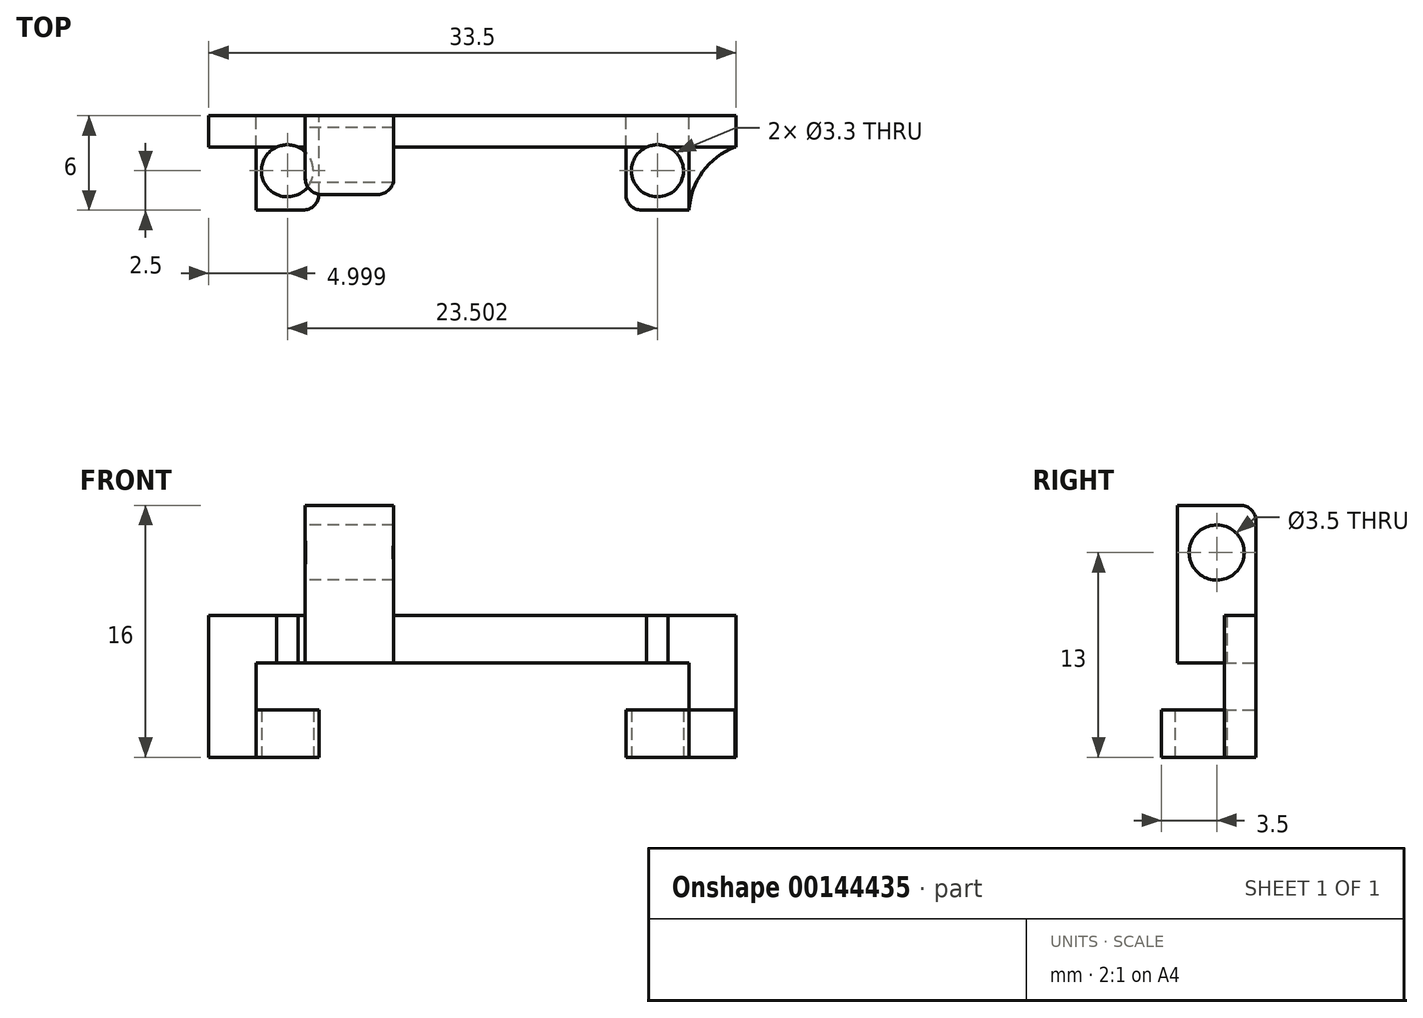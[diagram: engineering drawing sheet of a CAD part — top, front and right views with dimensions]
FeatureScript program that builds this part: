
annotation { "Feature Type Name" : "Feature", "Feature Type Description" : "" }
export const myFeature = defineFeature(function(context is Context, id is Id, definition is map)
    precondition{}
    {
        {
            var Q0;
            Q0=qCreatedBy(makeId("Front.planeOp"),FACE);
            var sketch = newSketch(context, id + "F0", { "sketchPlane" : qUnion([Q0])});
            skLineSegment(sketch, "E0.bottom", {"start": v(0, 0) * mm, "end": v(-16.75, 0) * mm});
            skLineSegment(sketch, "E0.top", {"start": v(0, 3) * mm, "end": v(-16.75, 3) * mm});
            skLineSegment(sketch, "E0.left", {"start": v(0, 0) * mm, "end": v(0, 3) * mm});
            skLineSegment(sketch, "E0.right", {"start": v(-16.75, 0) * mm, "end": v(-16.75, 3) * mm});
            skLineSegment(sketch, "E1.top", {"start": v(-16.75, 0) * mm, "end": v(-13.75, 0) * mm});
            skLineSegment(sketch, "E2.bottom", {"start": v(-13.75, 0) * mm, "end": v(-16.75, 0) * mm});
            skLineSegment(sketch, "E2.top", {"start": v(-13.75, -6) * mm, "end": v(-16.75, -6) * mm});
            skLineSegment(sketch, "E2.left", {"start": v(-13.75, 0) * mm, "end": v(-13.75, -6) * mm});
            skLineSegment(sketch, "E2.right", {"start": v(-16.75, 0) * mm, "end": v(-16.75, -6) * mm});
            skLineSegment(sketch, "E3.bottom", {"start": v(-9.75, -6) * mm, "end": v(-16.75, -6) * mm});
            skLineSegment(sketch, "E3.top", {"start": v(-9.75, -3) * mm, "end": v(-16.75, -3) * mm});
            skLineSegment(sketch, "E3.left", {"start": v(-16.75, -6) * mm, "end": v(-16.75, -3) * mm});
            skLineSegment(sketch, "E3.right", {"start": v(-9.75, -6) * mm, "end": v(-9.75, -3) * mm});
            skLineSegment(sketch, "E4.MirrorCS", {"start": v(0, 3) * mm, "end": v(16.75, 3) * mm});
            skLineSegment(sketch, "E5.MirrorCS", {"start": v(16.75, 0) * mm, "end": v(16.75, 3) * mm});
            skLineSegment(sketch, "E6.MirrorCS", {"start": v(16.75, 0) * mm, "end": v(16.75, -6) * mm});
            skLineSegment(sketch, "E7.MirrorCS", {"start": v(9.75, -3) * mm, "end": v(16.75, -3) * mm});
            skLineSegment(sketch, "E8.MirrorCS", {"start": v(9.75, -6) * mm, "end": v(9.75, -3) * mm});
            skLineSegment(sketch, "E9.MirrorCS", {"start": v(9.75, -6) * mm, "end": v(16.75, -6) * mm});
            skLineSegment(sketch, "E10.MirrorCS", {"start": v(13.75, -6) * mm, "end": v(16.75, -6) * mm});
            skLineSegment(sketch, "E11.MirrorCS", {"start": v(13.75, 0) * mm, "end": v(13.75, -6) * mm});
            skLineSegment(sketch, "E12.MirrorCS", {"start": v(0, 0) * mm, "end": v(16.75, 0) * mm});
            skSolve(sketch);
        }
        {
            var Q0;
            Q0=qSketchRegion(id+"F0",true);
            extrude(context, id + "F1", {"entities" : qUnion([Q0]), "depth" : 2 * mm});
        }
        {
            var Q0;
            Q0=makeQuery(id+"F1.opExtrude","CAP_FACE",FACE,{"disambiguationData":[OSD([sQuery(id+"F0.wireOp",EDGE,"E0.bottom"),sQuery(id+"F0.wireOp",EDGE,"E0.top"),sQuery(id+"F0.wireOp",EDGE,"aeqE6Dur-HZPA-TlM0-ftwt-VVeKIwCkpguP.bottom"),sQuery(id+"F0.wireOp",EDGE,"aeqE6Dur-HZPA-TlM0-ftwt-VVeKIwCkpguP.right"),sQuery(id+"F0.wireOp",EDGE,"3cbdc3cd-563d-4b25-9951-626386d711b80.MirrorCS"),sQuery(id+"F0.wireOp",EDGE,"b1a2d14d-5c19-498e-a2ee-c9adf1cd579e0.MirrorCS"),sQuery(id+"F0.wireOp",EDGE,"76f20797-3b26-4a3e-8da0-f82ea28bb6570.MirrorCS"),sQuery(id+"F0.wireOp",EDGE,"d48cfc68-1115-470f-a2cf-e761afef30250.MirrorCS"),sQuery(id+"F0.wireOp",EDGE,"421e91b7-741f-4417-84ce-826fcdc0de5d0.MirrorCS"),sQuery(id+"F0.wireOp",EDGE,"ea46c72d-2b80-4e23-a18a-e69fb02f9be50.MirrorCS"),sQuery(id+"F0.wireOp",EDGE,"2eb2be0c-9c20-47f0-8e2e-3a09440f1cf10.MirrorCS"),sQuery(id+"F0.wireOp",EDGE,"0540cde8-1ba2-4abf-b4bb-3b08df3cb87a0.MirrorCS"),sQuery(id+"F0.wireOp",EDGE,"018e8934-18b0-46ba-aa67-13de33aad30b0.MirrorCS"),sQuery(id+"F0.wireOp",EDGE,"1bcbefdf-3666-44cf-b95c-8deae155be0d0.MirrorCS"),sQuery(id+"F0.wireOp",EDGE,"05df909d-ea29-4b1f-aa96-9eb1370d7ef90.MirrorCS"),sQuery(id+"F0.wireOp",EDGE,"b368221b-3ff1-4703-9be4-a80ebce37bd50.MirrorCS"),sQuery(id+"F0.wireOp",EDGE,"785dab6b-0bc5-472c-b286-3d16cf4f01d00.MirrorCS")])],"isStart":false});
            var sketch = newSketch(context, id + "F2", { "sketchPlane" : qUnion([Q0])});
            skLineSegment(sketch, "E13.bottom", {"start": v(-9.75, -6) * mm, "end": v(-13.75, -6) * mm});
            skLineSegment(sketch, "E13.top", {"start": v(-9.75, -3) * mm, "end": v(-13.75, -3) * mm});
            skLineSegment(sketch, "E13.left", {"start": v(-13.75, -6) * mm, "end": v(-13.75, -3) * mm});
            skLineSegment(sketch, "E13.right", {"start": v(-9.75, -6) * mm, "end": v(-9.75, -3) * mm});
            skLineSegment(sketch, "E14.MirrorCS", {"start": v(9.75, -6) * mm, "end": v(9.75, -3) * mm});
            skLineSegment(sketch, "E15.MirrorCS", {"start": v(9.75, -3) * mm, "end": v(13.75, -3) * mm});
            skLineSegment(sketch, "E16.MirrorCS", {"start": v(13.75, -6) * mm, "end": v(13.75, -3) * mm});
            skLineSegment(sketch, "E17.MirrorCS", {"start": v(9.75, -6) * mm, "end": v(13.75, -6) * mm});
            skLineSegment(sketch, "E18", {"start": v(-13.75, -3) * mm, "end": v(-13.75, -6) * mm, "construction": true});
            skSolve(sketch);
        }
        {
            var Q0;
            Q0=qSketchRegion(id+"F2",true);
            extrude(context, id + "F3", {"entities" : qUnion([Q0]), "operationType" : NewBodyOperationType.ADD, "depth" : 4 * mm});
        }
        {
            var Q0;
            Q0=makeQuery(id+"F3.boolean.opBoolean","MERGE",FACE,{"derivedFrom":[makeQuery(id+"F1.opExtrude","SWEPT_FACE",FACE,{"disambiguationData":[OSD([sQuery(id+"F0.wireOp",EDGE,"d48cfc68-1115-470f-a2cf-e761afef30250.MirrorCS")])]}),makeQuery(id+"F3.opExtrude","SWEPT_FACE",FACE,{"disambiguationData":[OSD([sQuery(id+"F2.wireOp",EDGE,"E13.bottom")])]})]});
            var sketch = newSketch(context, id + "F4", { "sketchPlane" : qUnion([Q0])});
            skCircle(sketch, "E19", {"center": v(-11.75, 3.5) * mm, "radius": 1.65 * mm});
            skPoint(sketch, "E19.centerSnap0", {"position": v(-11.75, 6) * mm});
            skCircle(sketch, "E20.MirrorC", {"center": v(11.75, 3.5) * mm, "radius": 1.65 * mm});
            skSolve(sketch);
        }
        {
            var Q0;
            Q0=qSketchRegion(id+"F4",true);
            extrude(context, id + "F5", {"entities" : qUnion([Q0]), "operationType" : NewBodyOperationType.REMOVE, "endBound" : BoundingType.THROUGH_ALL, "oppositeDirection" : true, "depth" : 25.4 * mm});
        }
        {
            var Q0;
            Q0=makeQuery(id+"F1.opExtrude","SWEPT_FACE",FACE,{"disambiguationData":[OSD([sQuery(id+"F0.wireOp",EDGE,"E0.top"),sQuery(id+"F0.wireOp",EDGE,"E4.MirrorCS")])]});
            var sketch = newSketch(context, id + "F6", { "sketchPlane" : qUnion([Q0])});
            skLineSegment(sketch, "E21.bottom", {"start": v(-5, -2) * mm, "end": v(-10.61, -2) * mm});
            skLineSegment(sketch, "E21.top", {"start": v(-5, 0) * mm, "end": v(-10.61, 0) * mm});
            skLineSegment(sketch, "E21.left", {"start": v(-10.61, -2) * mm, "end": v(-10.61, 0) * mm});
            skLineSegment(sketch, "E21.right", {"start": v(-5, -2) * mm, "end": v(-5, 0) * mm});
            skLineSegment(sketch, "E22", {"start": v(0, -2) * mm, "end": v(0, 0) * mm, "construction": true});
            skSolve(sketch);
        }
        {
            var Q0;
            Q0 = qSketchRegion(id + "F6", true);
            extrude(context, id + "F7", {"entities" : qUnion([Q0]), "operationType" : NewBodyOperationType.ADD, "depth" : 7 * mm});
        }
        {
            var Q0;
            Q0=makeQuery(id+"F7.boolean.opBoolean","MERGE",FACE,{"derivedFrom":[makeQuery(id+"F1.opExtrude","CAP_FACE",FACE,{"disambiguationData":[OSD([sQuery(id+"F0.wireOp",EDGE,"E0.bottom"),sQuery(id+"F0.wireOp",EDGE,"E0.top"),sQuery(id+"F0.wireOp",EDGE,"E0.right"),sQuery(id+"F0.wireOp",EDGE,"E2.top"),sQuery(id+"F0.wireOp",EDGE,"E2.left"),sQuery(id+"F0.wireOp",EDGE,"E2.right"),sQuery(id+"F0.wireOp",EDGE,"E3.bottom"),sQuery(id+"F0.wireOp",EDGE,"E3.top"),sQuery(id+"F0.wireOp",EDGE,"E3.right"),sQuery(id+"F0.wireOp",EDGE,"E4.MirrorCS"),sQuery(id+"F0.wireOp",EDGE,"E5.MirrorCS"),sQuery(id+"F0.wireOp",EDGE,"E6.MirrorCS"),sQuery(id+"F0.wireOp",EDGE,"E7.MirrorCS"),sQuery(id+"F0.wireOp",EDGE,"E8.MirrorCS"),sQuery(id+"F0.wireOp",EDGE,"E9.MirrorCS"),sQuery(id+"F0.wireOp",EDGE,"E10.MirrorCS"),sQuery(id+"F0.wireOp",EDGE,"E11.MirrorCS"),sQuery(id+"F0.wireOp",EDGE,"E12.MirrorCS")])],"isStart":false}),makeQuery(id+"F7.opExtrude","SWEPT_FACE",FACE,{"disambiguationData":[OSD([sQuery(id+"F6.wireOp",EDGE,"E21.bottom")])]})]});
            var sketch = newSketch(context, id + "F8", { "sketchPlane" : qUnion([Q0])});
            skLineSegment(sketch, "E23.bottom", {"start": v(-5, 10) * mm, "end": v(-10.61, 10) * mm});
            skLineSegment(sketch, "E23.top", {"start": v(-5, 3) * mm, "end": v(-10.61, 3) * mm});
            skLineSegment(sketch, "E23.left", {"start": v(-10.61, 10) * mm, "end": v(-10.61, 3) * mm});
            skLineSegment(sketch, "E23.right", {"start": v(-5, 10) * mm, "end": v(-5, 3) * mm});
            skSolve(sketch);
        }
        {
            var Q0;
            Q0 = qSketchRegion(id + "F8", true);
            extrude(context, id + "F9", {"entities" : qUnion([Q0]), "operationType" : NewBodyOperationType.ADD, "depth" : 3 * mm});
        }
        {
            var Q0;
            Q0=makeQuery(id+"F9.boolean.opBoolean","MERGE",FACE,{"derivedFrom":[makeQuery(id+"F7.opExtrude","SWEPT_FACE",FACE,{"disambiguationData":[OSD([sQuery(id+"F6.wireOp",EDGE,"E21.left")])]}),makeQuery(id+"F9.opExtrude","SWEPT_FACE",FACE,{"disambiguationData":[OSD([sQuery(id+"F8.wireOp",EDGE,"E23.left")])]})]});
            var sketch = newSketch(context, id + "F10", { "sketchPlane" : qUnion([Q0])});
            skCircle(sketch, "E24", {"center": v(2.5, 7) * mm, "radius": 1.75 * mm});
            skPoint(sketch, "E24.centerSnap0", {"position": v(5, 6.5) * mm});
            skPoint(sketch, "E24.centerSnap1", {"position": v(2.5, 10) * mm});
            skSolve(sketch);
        }
        {
            var Q0;
            Q0 = qSketchRegion(id + "F10", true);
            extrude(context, id + "F11", {"entities" : qUnion([Q0]), "operationType" : NewBodyOperationType.REMOVE, "endBound" : BoundingType.THROUGH_ALL, "oppositeDirection" : true, "depth" : 25.4 * mm});
        }
        {
            var Q0;
            Q0=makeQuery(id+"F9.opExtrude","CAP_EDGE",EDGE,{"disambiguationData":[OSD([sQuery(id+"F8.wireOp",EDGE,"E23.left")])],"isStart":false});
            var Q1;
            Q1=makeQuery(id+"F9.opExtrude","CAP_EDGE",EDGE,{"disambiguationData":[OSD([sQuery(id+"F8.wireOp",EDGE,"E23.right")])],"isStart":false});
            fillet(context, id + "F12", {"entities" : qUnion([Q0, Q1]), "radius" : 1 * mm, "tangentPropagation" : true, "allowEdgeOverflow" : false});
        }
        {
            var Q0;
            Q0=makeQuery(id+"F9.opExtrude","SWEPT_FACE",FACE,{"disambiguationData":[OSD([sQuery(id+"F8.wireOp",EDGE,"E23.top")])]});
            var sketch = newSketch(context, id + "F13", { "sketchPlane" : qUnion([Q0])});
            skLineSegment(sketch, "E25", {"start": v(-7.8, 5) * mm, "end": v(-6, 5) * mm});
            skLineSegment(sketch, "E26", {"start": v(-7.8, 5) * mm, "end": v(-7.8, 2) * mm, "construction": true});
            skLineSegment(sketch, "E27.MirrorCS", {"start": v(-7.8, 5) * mm, "end": v(-9.61, 5) * mm});
            skLineSegment(sketch, "E28", {"start": v(-5, 4) * mm, "end": v(-5, 2) * mm});
            skLineSegment(sketch, "E29.MirrorCS", {"start": v(-10.61, 4) * mm, "end": v(-10.61, 2) * mm});
            skArc(sketch, "E30", {"start": v(-9.61, 5) * mm, "mid": v(-10.32, 4.7) * mm, "end": v(-10.61, 4) * mm});
            skArc(sketch, "E31.MirrorCS", {"start": v(-6, 5) * mm, "mid": v(-5.3, 4.7) * mm, "end": v(-5, 4) * mm});
            skSolve(sketch);
        }
        {
            var Q0;
            Q0=makeQuery(id+"F13.imprint","IMPRINT",FACE,{"disambiguationData":[TD([[makeQuery(id+"F13.imprint","IMPRINT",EDGE,{"derivedFrom":sQuery(id+"F13.wireOp",EDGE,"E25")}),1.0]])]});
            var Q1;
            Q1=makeQuery(id+"F1.opExtrude","SWEPT_FACE",FACE,{"disambiguationData":[OSD([sQuery(id+"F0.wireOp",EDGE,"E0.bottom"),sQuery(id+"F0.wireOp",EDGE,"E12.MirrorCS")])]});
            extrude(context, id + "F14", {"entities" : qUnion([Q0]), "operationType" : NewBodyOperationType.ADD, "endBound" : BoundingType.UP_TO_SURFACE, "endBoundEntityFace" : qUnion([Q1]), "depth" : 25.4 * mm});
        }
        {
            var Q0;
            Q0=makeQuery(id+"F3.boolean.opBoolean","MERGE",FACE,{"derivedFrom":[makeQuery(id+"F1.opExtrude","SWEPT_FACE",FACE,{"disambiguationData":[OSD([sQuery(id+"F0.wireOp",EDGE,"E7.MirrorCS")])]}),makeQuery(id+"F3.opExtrude","SWEPT_FACE",FACE,{"disambiguationData":[OSD([sQuery(id+"F2.wireOp",EDGE,"E15.MirrorCS")])]})]});
            var sketch = newSketch(context, id + "F15", { "sketchPlane" : qUnion([Q0])});
            skArc(sketch, "E32", {"start": v(16.69, -2) * mm, "mid": v(14.63, -3.56) * mm, "end": v(13.75, -6) * mm});
            skArc(sketch, "E33.MirrorCS", {"start": v(-16.69, -2) * mm, "mid": v(-14.63, -3.56) * mm, "end": v(-13.75, -6) * mm});
            skLineSegment(sketch, "E34", {"start": v(16.69, -2) * mm, "end": v(13.75, -2) * mm});
            skLineSegment(sketch, "E35", {"start": v(13.75, -2) * mm, "end": v(13.75, -6) * mm});
            skLineSegment(sketch, "E36.MirrorCS", {"start": v(-13.75, -2) * mm, "end": v(-13.75, -6) * mm});
            skLineSegment(sketch, "E37.MirrorCS", {"start": v(-16.69, -2) * mm, "end": v(-13.75, -2) * mm});
            skSolve(sketch);
        }
        {
            var Q0;
            Q0=makeQuery(id+"F15.imprint","IMPRINT",FACE,{"disambiguationData":[TD([[makeQuery(id+"F15.imprint","IMPRINT",EDGE,{"derivedFrom":sQuery(id+"F15.wireOp",EDGE,"E33.MirrorCS")}),1.0]])]});
            var Q1;
            Q1=makeQuery(id+"F15.imprint","IMPRINT",FACE,{"disambiguationData":[TD([[makeQuery(id+"F15.imprint","IMPRINT",EDGE,{"derivedFrom":sQuery(id+"F15.wireOp",EDGE,"E32")}),-1.0]])]});
            var Q2;
            Q2=makeQuery(id+"F3.boolean.opBoolean","MERGE",FACE,{"derivedFrom":[makeQuery(id+"F1.opExtrude","SWEPT_FACE",FACE,{"disambiguationData":[OSD([sQuery(id+"F0.wireOp",EDGE,"E9.MirrorCS"),sQuery(id+"F0.wireOp",EDGE,"E10.MirrorCS")])]}),makeQuery(id+"F3.opExtrude","SWEPT_FACE",FACE,{"disambiguationData":[OSD([sQuery(id+"F2.wireOp",EDGE,"E17.MirrorCS")])]})]});
            extrude(context, id + "F16", {"entities" : qUnion([Q0, Q1]), "endBound" : BoundingType.UP_TO_SURFACE, "oppositeDirection" : true, "endBoundEntityFace" : qUnion([Q2]), "depth" : 25.4 * mm});
        }
        {
            var Q0;
            Q0=makeQuery(id+"F3.opExtrude","CAP_EDGE",EDGE,{"disambiguationData":[OSD([sQuery(id+"F2.wireOp",EDGE,"E13.right")])],"isStart":false});
            var Q1;
            Q1=makeQuery(id+"F3.opExtrude","CAP_EDGE",EDGE,{"disambiguationData":[OSD([sQuery(id+"F2.wireOp",EDGE,"E14.MirrorCS")])],"isStart":false});
            fillet(context, id + "F17", {"entities" : qUnion([Q0, Q1]), "radius" : 1 * mm, "tangentPropagation" : true, "allowEdgeOverflow" : false});
        }
        {
            var Q0;
            Q0=makeQuery(id+"F7.opExtrude","CAP_EDGE",EDGE,{"disambiguationData":[OSD([sQuery(id+"F6.wireOp",EDGE,"E21.top")])],"isStart":false});
            fillet(context, id + "F18", {"entities" : qUnion([Q0]), "radius" : 1 * mm, "tangentPropagation" : true, "allowEdgeOverflow" : false});
        }
    });
